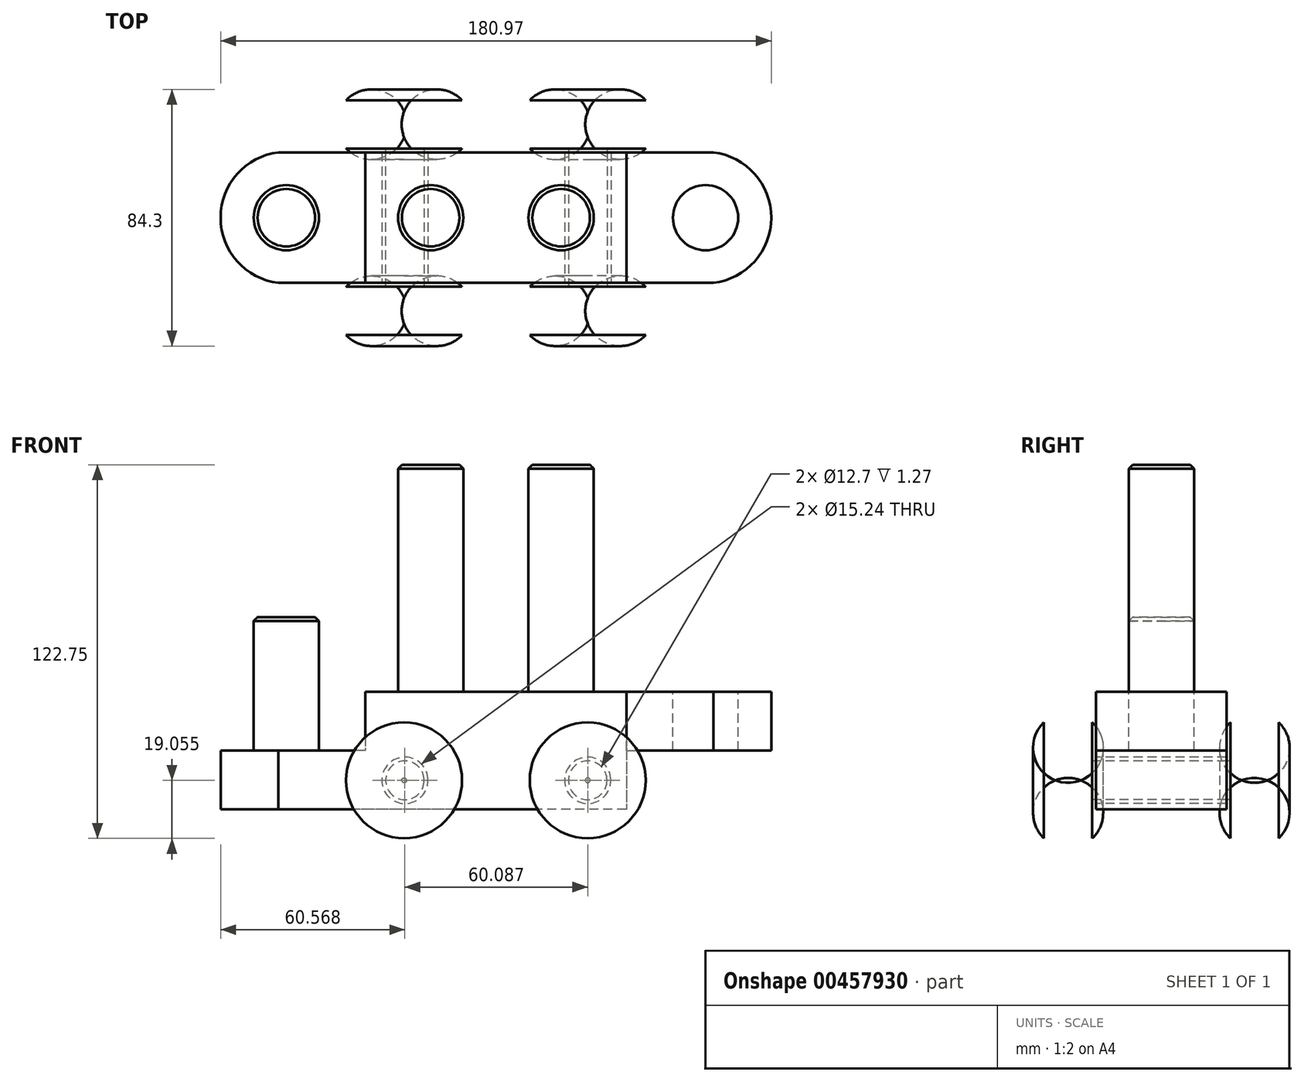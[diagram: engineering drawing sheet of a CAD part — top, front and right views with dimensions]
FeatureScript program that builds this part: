
annotation { "Feature Type Name" : "Feature", "Feature Type Description" : "" }
export const myFeature = defineFeature(function(context is Context, id is Id, definition is map)
    precondition{}
    {
        {
            var Q0;
            Q0=qCreatedBy(makeId("Top.planeOp"),FACE);
            var sketch = newSketch(context, id + "F0", { "sketchPlane" : qUnion([Q0])});
            skLineSegment(sketch, "E0.bottom", {"start": v(42.88, 21.44) * mm, "end": v(-42.88, 21.44) * mm});
            skLineSegment(sketch, "E0.top", {"start": v(42.88, -21.44) * mm, "end": v(-42.88, -21.44) * mm});
            skLineSegment(sketch, "E0.left", {"start": v(42.88, 21.44) * mm, "end": v(42.88, -21.44) * mm});
            skLineSegment(sketch, "E0.right", {"start": v(-42.88, 21.44) * mm, "end": v(-42.88, -21.44) * mm});
            skPoint(sketch, "E0.middle", {"position": v(0, 0) * mm});
            skLineSegment(sketch, "E1", {"start": v(-42.88, 0) * mm, "end": v(0, 0) * mm, "construction": true});
            skCircle(sketch, "E2", {"center": v(-21.44, 0) * mm, "radius": 10.72 * mm});
            skLineSegment(sketch, "E3", {"start": v(0, 0) * mm, "end": v(42.88, 0) * mm, "construction": true});
            skCircle(sketch, "E4", {"center": v(21.44, 0) * mm, "radius": 10.72 * mm});
            skSolve(sketch);
        }
        {
            var Q0;
            Q0=makeQuery(id+"F0.imprint","IMPRINT",FACE,{"disambiguationData":[TD([[makeQuery(id+"F0.imprint","IMPRINT",EDGE,{"derivedFrom":sQuery(id+"F0.wireOp",EDGE,"E2")}),1.0]])]});
            var Q1;
            Q1=makeQuery(id+"F0.imprint","IMPRINT",FACE,{"disambiguationData":[TD([[makeQuery(id+"F0.imprint","IMPRINT",EDGE,{"derivedFrom":sQuery(id+"F0.wireOp",EDGE,"E4")}),1.0]])]});
            var Q2;
            Q2=makeQuery(id+"F0.imprint","IMPRINT",FACE,{"disambiguationData":[TD([[makeQuery(id+"F0.imprint","IMPRINT",EDGE,{"derivedFrom":sQuery(id+"F0.wireOp",EDGE,"E0.bottom")}),1.0]])]});
            extrude(context, id + "F1", {"entities" : qUnion([Q0, Q1, Q2]), "depth" : 38.6 * mm, "offsetDistance" : 25.4 * mm});
        }
        {
            var Q0;
            Q0=makeQuery(id+"F1.opExtrude","CAP_FACE",FACE,{"disambiguationData":[OSD([sQuery(id+"F0.wireOp",EDGE,"E0.bottom"),sQuery(id+"F0.wireOp",EDGE,"E0.top"),sQuery(id+"F0.wireOp",EDGE,"E0.left"),sQuery(id+"F0.wireOp",EDGE,"E0.right")])],"isStart":false});
            var sketch = newSketch(context, id + "F2", { "sketchPlane" : qUnion([Q0])});
            skCircle(sketch, "E5", {"center": v(21.44, 0) * mm, "radius": 10.72 * mm});
            skCircle(sketch, "E6", {"center": v(-21.44, 0) * mm, "radius": 10.72 * mm});
            skPoint(sketch, "E7.end.orphan", {"position": v(42.88, 0) * mm});
            skPoint(sketch, "E8.orphan", {"position": v(0, 0) * mm});
            skPoint(sketch, "E9.end.orphan", {"position": v(-42.88, 0) * mm});
            skSolve(sketch);
        }
        {
            var Q0;
            Q0=makeQuery(id+"F2.imprint","IMPRINT",FACE,{"disambiguationData":[TD([[makeQuery(id+"F2.imprint","IMPRINT",EDGE,{"derivedFrom":sQuery(id+"F2.wireOp",EDGE,"E6")}),1.0]])]});
            var Q1;
            Q1=makeQuery(id+"F2.imprint","IMPRINT",FACE,{"disambiguationData":[TD([[makeQuery(id+"F2.imprint","IMPRINT",EDGE,{"derivedFrom":sQuery(id+"F2.wireOp",EDGE,"E5")}),1.0]])]});
            extrude(context, id + "F3", {"entities" : qUnion([Q0, Q1]), "operationType" : NewBodyOperationType.ADD, "depth" : 74.61 * mm, "offsetDistance" : 25.4 * mm});
        }
        {
            var Q0;
            Q0=makeQuery(id+"F1.opExtrude","CAP_FACE",FACE,{"disambiguationData":[OSD([sQuery(id+"F0.wireOp",EDGE,"E0.bottom"),sQuery(id+"F0.wireOp",EDGE,"E0.top"),sQuery(id+"F0.wireOp",EDGE,"E0.left"),sQuery(id+"F0.wireOp",EDGE,"E0.right")])],"isStart":false});
            var sketch = newSketch(context, id + "F4", { "sketchPlane" : qUnion([Q0])});
            skLineSegment(sketch, "E10", {"start": v(42.88, -21.44) * mm, "end": v(71.45, -21.44) * mm});
            skLineSegment(sketch, "E11", {"start": v(42.88, 21.44) * mm, "end": v(71.45, 21.44) * mm});
            skArc(sketch, "E12", {"start": v(71.45, -21.44) * mm, "mid": v(90.5, 0) * mm, "end": v(71.45, 21.44) * mm});
            skCircle(sketch, "E13", {"center": v(68.9, 0) * mm, "radius": 10.72 * mm});
            skPoint(sketch, "E14.orphan", {"position": v(42.88, 0) * mm});
            skLineSegment(sketch, "E15.trimOffspring", {"start": v(79.62, 0) * mm, "end": v(90.5, 0) * mm, "construction": true});
            skSolve(sketch);
        }
        {
            var Q0;
            Q0=makeQuery(id+"F4.imprint","IMPRINT",FACE,{"disambiguationData":[TD([[makeQuery(id+"F4.imprint","IMPRINT",EDGE,{"derivedFrom":sQuery(id+"F4.wireOp",EDGE,"E10")}),1.0]])]});
            extrude(context, id + "F5", {"entities" : qUnion([Q0]), "oppositeDirection" : true, "depth" : 19.3 * mm, "offsetDistance" : 25.4 * mm});
        }
        {
            var Q0;
            Q0=makeQuery(id+"F1.opExtrude","CAP_FACE",FACE,{"disambiguationData":[OSD([sQuery(id+"F0.wireOp",EDGE,"E0.bottom"),sQuery(id+"F0.wireOp",EDGE,"E0.top"),sQuery(id+"F0.wireOp",EDGE,"E0.left"),sQuery(id+"F0.wireOp",EDGE,"E0.right")])],"isStart":true});
            var sketch = newSketch(context, id + "F6", { "sketchPlane" : qUnion([Q0])});
            skLineSegment(sketch, "E16", {"start": v(-42.88, -21.44) * mm, "end": v(-71.45, -21.44) * mm});
            skLineSegment(sketch, "E17", {"start": v(-42.88, 21.44) * mm, "end": v(-71.45, 21.44) * mm});
            skArc(sketch, "E18", {"start": v(-71.45, 21.44) * mm, "mid": v(-90.48, 0) * mm, "end": v(-71.45, -21.44) * mm});
            skCircle(sketch, "E19", {"center": v(-68.89, 0) * mm, "radius": 10.72 * mm});
            skSolve(sketch);
        }
        {
            var Q0;
            Q0=makeQuery(id+"F6.imprint","IMPRINT",FACE,{"disambiguationData":[TD([[makeQuery(id+"F6.imprint","IMPRINT",EDGE,{"derivedFrom":sQuery(id+"F6.wireOp",EDGE,"E19")}),1.0]])]});
            extrude(context, id + "F7", {"entities" : qUnion([Q0]), "oppositeDirection" : true, "depth" : 63.2 * mm, "offsetDistance" : 25.4 * mm});
        }
        {
            var Q0;
            Q0=makeQuery(id+"F6.imprint","IMPRINT",FACE,{"disambiguationData":[TD([[makeQuery(id+"F6.imprint","IMPRINT",EDGE,{"derivedFrom":sQuery(id+"F6.wireOp",EDGE,"E16")}),-1.0]])]});
            extrude(context, id + "F8", {"entities" : qUnion([Q0]), "operationType" : NewBodyOperationType.ADD, "oppositeDirection" : true, "depth" : 19.3 * mm, "offsetDistance" : 25.4 * mm});
        }
        {
            var Q0;
            Q0=makeQuery(id+"F3.opExtrude","CAP_FACE",FACE,{"disambiguationData":[OSD([sQuery(id+"F2.wireOp",EDGE,"E6")])],"isStart":false});
            chamfer(context, id + "F9", {"entities" : qUnion([Q0]), "width" : 1.27 * mm, "tangentPropagation" : true});
        }
        {
            var Q0;
            Q0=makeQuery(id+"F3.opExtrude","CAP_FACE",FACE,{"disambiguationData":[OSD([sQuery(id+"F2.wireOp",EDGE,"E5")])],"isStart":false});
            chamfer(context, id + "F10", {"entities" : qUnion([Q0]), "width" : 1.27 * mm, "tangentPropagation" : true});
        }
        {
            var Q0;
            Q0=makeQuery(id+"F7.opExtrude","CAP_FACE",FACE,{"disambiguationData":[OSD([sQuery(id+"F6.wireOp",EDGE,"E19")])],"isStart":false});
            chamfer(context, id + "F11", {"entities" : qUnion([Q0]), "width" : 1.27 * mm, "tangentPropagation" : true});
        }
        {
            var Q0;
            Q0=makeQuery(id+"F1.opExtrude","SWEPT_FACE",FACE,{"disambiguationData":[OSD([sQuery(id+"F0.wireOp",EDGE,"E0.top")])]});
            var sketch = newSketch(context, id + "F12", { "sketchPlane" : qUnion([Q0])});
            skCircle(sketch, "E20", {"center": v(-29.91, 9.52) * mm, "radius": 6.35 * mm});
            skPoint(sketch, "E21.orphan", {"position": v(42.88, 9.53) * mm});
            skCircle(sketch, "E22", {"center": v(30.18, 9.53) * mm, "radius": 6.35 * mm});
            skCircle(sketch, "E23.0", {"center": v(-29.91, 9.52) * mm, "radius": 7.62 * mm});
            skCircle(sketch, "E24.0", {"center": v(30.18, 9.53) * mm, "radius": 7.62 * mm});
            skCircle(sketch, "E25", {"center": v(30.18, 9.53) * mm, "radius": 0.01 * mm});
            skLineSegment(sketch, "E26", {"start": v(-29.91, 9.52) * mm, "end": v(30.18, 9.52) * mm, "construction": true});
            skSolve(sketch);
        }
        {
            var Q0;
            Q0=makeQuery(id+"F12.imprint","IMPRINT",FACE,{"disambiguationData":[TD([[makeQuery(id+"F12.imprint","IMPRINT",EDGE,{"derivedFrom":sQuery(id+"F12.wireOp",EDGE,"E20")}),-1.0]])]});
            var Q1;
            Q1=makeQuery(id+"F12.imprint","IMPRINT",FACE,{"disambiguationData":[TD([[makeQuery(id+"F12.imprint","IMPRINT",EDGE,{"derivedFrom":sQuery(id+"F12.wireOp",EDGE,"E22")}),-1.0]])]});
            var Q2;
            Q2=makeQuery(id+"F1.opExtrude","SWEPT_FACE",FACE,{"disambiguationData":[OSD([sQuery(id+"F0.wireOp",EDGE,"E0.bottom")])]});
            extrude(context, id + "F13", {"entities" : qUnion([Q0, Q1]), "operationType" : NewBodyOperationType.REMOVE, "endBound" : BoundingType.UP_TO_SURFACE, "oppositeDirection" : true, "endBoundEntityFace" : qUnion([Q2]), "depth" : 25.4 * mm, "offsetDistance" : 25.4 * mm});
        }
        {
            var Q0;
            Q0=makeQuery(id+"F13.boolean.opBoolean","SPLIT",FACE,{"disambiguationData":[TD([makeQuery(id+"F13.opExtrude","SWEPT_FACE",FACE,{"disambiguationData":[OSD([sQuery(id+"F12.wireOp",EDGE,"E20")])]})])],"derivedFrom":makeQuery(id+"F1.opExtrude","SWEPT_FACE",FACE,{"disambiguationData":[OSD([sQuery(id+"F0.wireOp",EDGE,"E0.top")])]})});
            var Q1;
            Q1=makeQuery(id+"F13.boolean.opBoolean","SPLIT",FACE,{"disambiguationData":[TD([makeQuery(id+"F13.opExtrude","SWEPT_FACE",FACE,{"disambiguationData":[OSD([sQuery(id+"F12.wireOp",EDGE,"E22")])]})])],"derivedFrom":makeQuery(id+"F1.opExtrude","SWEPT_FACE",FACE,{"disambiguationData":[OSD([sQuery(id+"F0.wireOp",EDGE,"E0.top")])]})});
            extrude(context, id + "F14", {"entities" : qUnion([Q0, Q1]), "operationType" : NewBodyOperationType.ADD, "depth" : 1.27 * mm, "offsetDistance" : 25.4 * mm});
        }
        {
            var Q0;
            Q0=makeQuery(id+"F13.boolean.opBoolean","SPLIT",FACE,{"disambiguationData":[TD([makeQuery(id+"F13.opExtrude","SWEPT_FACE",FACE,{"disambiguationData":[OSD([sQuery(id+"F12.wireOp",EDGE,"E22")])]})])],"derivedFrom":makeQuery(id+"F1.opExtrude","SWEPT_FACE",FACE,{"disambiguationData":[OSD([sQuery(id+"F0.wireOp",EDGE,"E0.bottom")])]})});
            var Q1;
            Q1=makeQuery(id+"F13.boolean.opBoolean","SPLIT",FACE,{"disambiguationData":[TD([makeQuery(id+"F13.opExtrude","SWEPT_FACE",FACE,{"disambiguationData":[OSD([sQuery(id+"F12.wireOp",EDGE,"E20")])]})])],"derivedFrom":makeQuery(id+"F1.opExtrude","SWEPT_FACE",FACE,{"disambiguationData":[OSD([sQuery(id+"F0.wireOp",EDGE,"E0.bottom")])]})});
            extrude(context, id + "F15", {"entities" : qUnion([Q0, Q1]), "depth" : 1.27 * mm, "offsetDistance" : 25.4 * mm});
        }
        {
            var Q0;
            Q0=sQuery(id+"F12.wireOp",EDGE,"E26");
            cPlane(context, id + "F16", {"entities" : qUnion([Q0]), "cplaneType" : CPlaneType.LINE_ANGLE, "offset" : 25.4 * mm, "angle" : 90 * degree, "width" : 152.4 * mm, "height" : 152.4 * mm});
        }
        {
            var Q0;
            Q0=qCreatedBy(id+"F16.planeOp",FACE);
            var sketch = newSketch(context, id + "F17", { "sketchPlane" : qUnion([Q0])});
            skLineSegment(sketch, "E27", {"start": v(-29.91, -21.44) * mm, "end": v(-29.91, 26.7) * mm, "construction": true});
            skLineSegment(sketch, "E28", {"start": v(30.18, -21.44) * mm, "end": v(30.18, 22.7) * mm, "construction": true});
            skLineSegment(sketch, "E29", {"start": v(30.18, -21.44) * mm, "end": v(30.18, -22.7) * mm});
            skLineSegment(sketch, "E30", {"start": v(30.18, -38.58) * mm, "end": v(49.23, -38.58) * mm});
            skLineSegment(sketch, "E31", {"start": v(30.18, -21.44) * mm, "end": v(49.23, -21.44) * mm});
            skPoint(sketch, "E32.orphan", {"position": v(30.18, -30.01) * mm});
            skLineSegment(sketch, "E33", {"start": v(30.18, -22.7) * mm, "end": v(49.23, -22.7) * mm});
            skLineSegment(sketch, "E34", {"start": v(30.18, -22.7) * mm, "end": v(30.18, -38.58) * mm});
            skArc(sketch, "E35", {"start": v(49.23, -38.58) * mm, "mid": v(52.4, -30.65) * mm, "end": v(49.23, -22.7) * mm});
            skPoint(sketch, "E36.orphan", {"position": v(30.18, -30.65) * mm});
            skLineSegment(sketch, "E37.MirrorCS", {"start": v(30.18, 22.7) * mm, "end": v(49.23, 22.7) * mm});
            skArc(sketch, "E38.MirrorCS", {"start": v(49.23, 38.58) * mm, "mid": v(52.4, 30.65) * mm, "end": v(49.23, 22.7) * mm});
            skLineSegment(sketch, "E39.MirrorCS", {"start": v(30.18, 38.58) * mm, "end": v(49.23, 38.58) * mm});
            skLineSegment(sketch, "E40.MirrorCS", {"start": v(30.18, 22.7) * mm, "end": v(30.18, 38.58) * mm});
            skLineSegment(sketch, "E41.MirrorCS", {"start": v(-30.18, 38.58) * mm, "end": v(-49.23, 38.58) * mm});
            skArc(sketch, "E42.MirrorCS", {"start": v(-49.23, 38.58) * mm, "mid": v(-52.4, 30.65) * mm, "end": v(-49.23, 22.7) * mm});
            skLineSegment(sketch, "E43.MirrorCS", {"start": v(-30.18, 22.7) * mm, "end": v(-49.23, 22.7) * mm});
            skLineSegment(sketch, "E44.MirrorCS", {"start": v(-30.18, -22.7) * mm, "end": v(-30.18, -38.58) * mm});
            skLineSegment(sketch, "E45.MirrorCS", {"start": v(-30.18, -38.58) * mm, "end": v(-49.23, -38.58) * mm});
            skLineSegment(sketch, "E46.MirrorCS", {"start": v(-30.18, -22.7) * mm, "end": v(-49.23, -22.7) * mm});
            skArc(sketch, "E47.MirrorCS", {"start": v(-49.23, -38.58) * mm, "mid": v(-52.4, -30.65) * mm, "end": v(-49.23, -22.7) * mm});
            skLineSegment(sketch, "E48.trimOffspring", {"start": v(30.18, 38.58) * mm, "end": v(30.18, 49.4) * mm, "construction": true});
            skLineSegment(sketch, "E49.MirrorCS", {"start": v(-30.18, 22.7) * mm, "end": v(-30.18, 38.58) * mm});
            skSolve(sketch);
        }
        {
            var Q0;
            Q0=makeQuery(id+"F17.imprint","IMPRINT",FACE,{"disambiguationData":[TD([[makeQuery(id+"F17.imprint","IMPRINT",EDGE,{"derivedFrom":sQuery(id+"F17.wireOp",EDGE,"E30")}),1.0]])]});
            var Q1;
            Q1=makeQuery(id+"F14.opExtrude","CAP_EDGE",EDGE,{"disambiguationData":[OSD([sQuery(id+"F12.wireOp",EDGE,"E22")])],"isStart":false});
            revolve(context, id + "F18", {"entities" : qUnion([Q0]), "axis" : qUnion([Q1]), "revolveType" : RevolveType.FULL});
        }
        {
            var Q0;
            Q0=makeQuery(id+"F17.imprint","IMPRINT",FACE,{"disambiguationData":[TD([[makeQuery(id+"F17.imprint","IMPRINT",EDGE,{"derivedFrom":sQuery(id+"F17.wireOp",EDGE,"E37.MirrorCS")}),1.0]])]});
            var Q1;
            Q1=sQuery(id+"F17.wireOp",EDGE,"E40.MirrorCS");
            revolve(context, id + "F19", {"operationType" : NewBodyOperationType.ADD, "entities" : qUnion([Q0]), "axis" : qUnion([Q1]), "revolveType" : RevolveType.FULL});
        }
        {
            var Q0;
            Q0=makeQuery(id+"F17.imprint","IMPRINT",FACE,{"disambiguationData":[TD([[makeQuery(id+"F17.imprint","IMPRINT",EDGE,{"derivedFrom":sQuery(id+"F17.wireOp",EDGE,"E41.MirrorCS")}),1.0]])]});
            var Q1;
            Q1=sQuery(id+"F17.wireOp",EDGE,"E49.MirrorCS");
            revolve(context, id + "F20", {"operationType" : NewBodyOperationType.ADD, "entities" : qUnion([Q0]), "axis" : qUnion([Q1]), "revolveType" : RevolveType.FULL});
        }
        {
            var Q0;
            Q0=makeQuery(id+"F17.imprint","IMPRINT",FACE,{"disambiguationData":[TD([[makeQuery(id+"F17.imprint","IMPRINT",EDGE,{"derivedFrom":sQuery(id+"F17.wireOp",EDGE,"E44.MirrorCS")}),-1.0]])]});
            var Q1;
            Q1=sQuery(id+"F17.wireOp",EDGE,"E44.MirrorCS");
            revolve(context, id + "F21", {"operationType" : NewBodyOperationType.ADD, "entities" : qUnion([Q0]), "axis" : qUnion([Q1]), "revolveType" : RevolveType.FULL});
        }
    });
